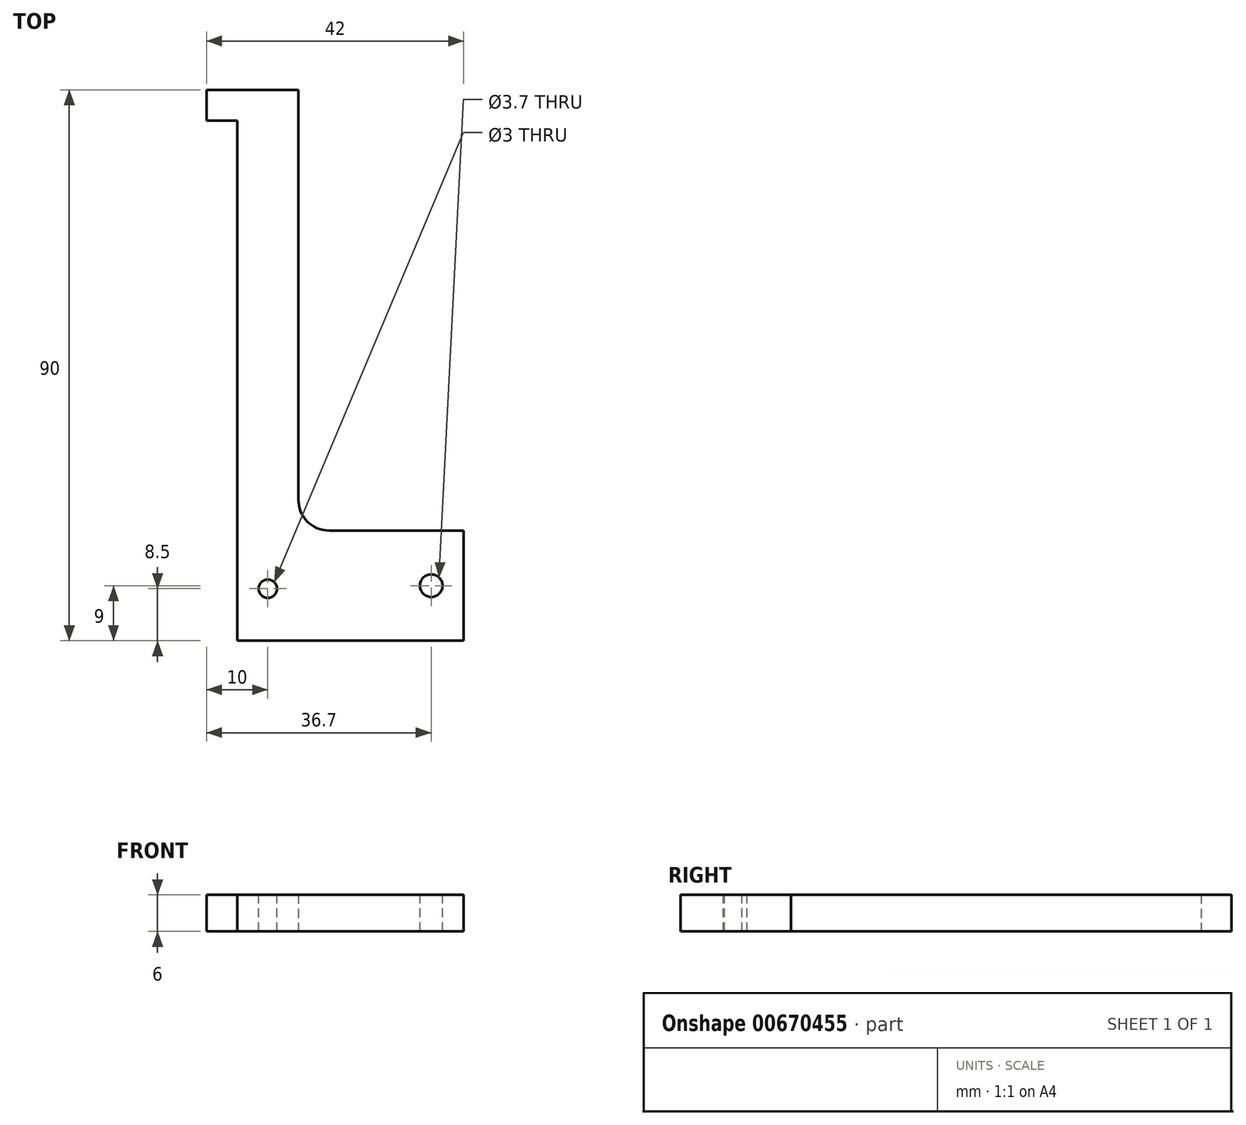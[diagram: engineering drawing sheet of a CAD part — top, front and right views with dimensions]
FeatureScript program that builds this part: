
annotation { "Feature Type Name" : "Feature", "Feature Type Description" : "" }
export const myFeature = defineFeature(function(context is Context, id is Id, definition is map)
    precondition{}
    {
        {
            var Q0;
            Q0=qCreatedBy(makeId("Top.planeOp"),FACE);
            var sketch = newSketch(context, id + "F0", { "sketchPlane" : qUnion([Q0])});
            skLineSegment(sketch, "E0.bottom", {"start": v(18.5, -9) * mm, "end": v(-18.5, -9) * mm});
            skLineSegment(sketch, "E0.top", {"start": v(18.5, 9) * mm, "end": v(1.5, 9) * mm});
            skLineSegment(sketch, "E0.left", {"start": v(18.5, -9) * mm, "end": v(18.5, 9) * mm});
            skLineSegment(sketch, "E0.right", {"start": v(-18.5, -9) * mm, "end": v(-18.5, 9) * mm});
            skPoint(sketch, "E0.middle", {"position": v(0, 0) * mm});
            skPoint(sketch, "E1.right.end.orphan", {"position": v(0, 45) * mm});
            skLineSegment(sketch, "E2", {"start": v(-3.5, 9) * mm, "end": v(1.5, 9) * mm});
            skLineSegment(sketch, "E3.left", {"start": v(-18.5, 9) * mm, "end": v(-18.5, 76) * mm});
            skLineSegment(sketch, "E4.bottom", {"start": v(-18.5, 81) * mm, "end": v(-23.5, 81) * mm});
            skLineSegment(sketch, "E4.top", {"start": v(-18.5, 76) * mm, "end": v(-23.5, 76) * mm});
            skLineSegment(sketch, "E4.right", {"start": v(-23.5, 81) * mm, "end": v(-23.5, 76) * mm});
            skLineSegment(sketch, "E5", {"start": v(-18.5, 81) * mm, "end": v(-8.5, 81) * mm});
            skLineSegment(sketch, "E6", {"start": v(-8.5, 81) * mm, "end": v(-8.5, 14) * mm});
            skPoint(sketch, "E7.visualSharp", {"position": v(-8.5, 9) * mm});
            skArc(sketch, "E7.filletArc", {"start": v(-8.5, 14) * mm, "mid": v(-7.04, 10.46) * mm, "end": v(-3.5, 9) * mm});
            skSolve(sketch);
        }
        {
            var Q0;
            Q0 = qSketchRegion(id + "F0", true);
            extrude(context, id + "F1", {"entities" : qUnion([Q0]), "depth" : 6 * mm, "offsetDistance" : 25 * mm});
        }
        {
            var Q0;
            Q0=makeQuery(id+"F1.opExtrude","CAP_FACE",FACE,{"disambiguationData":[OSD([sQuery(id+"F0.wireOp",EDGE,"E0.bottom"),sQuery(id+"F0.wireOp",EDGE,"E0.top"),sQuery(id+"F0.wireOp",EDGE,"E0.left"),sQuery(id+"F0.wireOp",EDGE,"E0.right"),sQuery(id+"F0.wireOp",EDGE,"E2"),sQuery(id+"F0.wireOp",EDGE,"E3.left"),sQuery(id+"F0.wireOp",EDGE,"E4.bottom"),sQuery(id+"F0.wireOp",EDGE,"E4.top"),sQuery(id+"F0.wireOp",EDGE,"E4.right"),sQuery(id+"F0.wireOp",EDGE,"E5"),sQuery(id+"F0.wireOp",EDGE,"E6"),sQuery(id+"F0.wireOp",EDGE,"E7.filletArc")])],"isStart":false});
            var sketch = newSketch(context, id + "F2", { "sketchPlane" : qUnion([Q0])});
            skCircle(sketch, "E8", {"center": v(-13.5, -0.5) * mm, "radius": 1.5 * mm});
            skCircle(sketch, "E9", {"center": v(13.2, 0) * mm, "radius": 1.85 * mm});
            skSolve(sketch);
        }
        {
            var Q0;
            Q0 = qSketchRegion(id + "F2", true);
            extrude(context, id + "F3", {"entities" : qUnion([Q0]), "operationType" : NewBodyOperationType.REMOVE, "oppositeDirection" : true, "depth" : 25 * mm, "offsetDistance" : 25 * mm});
        }
    });
